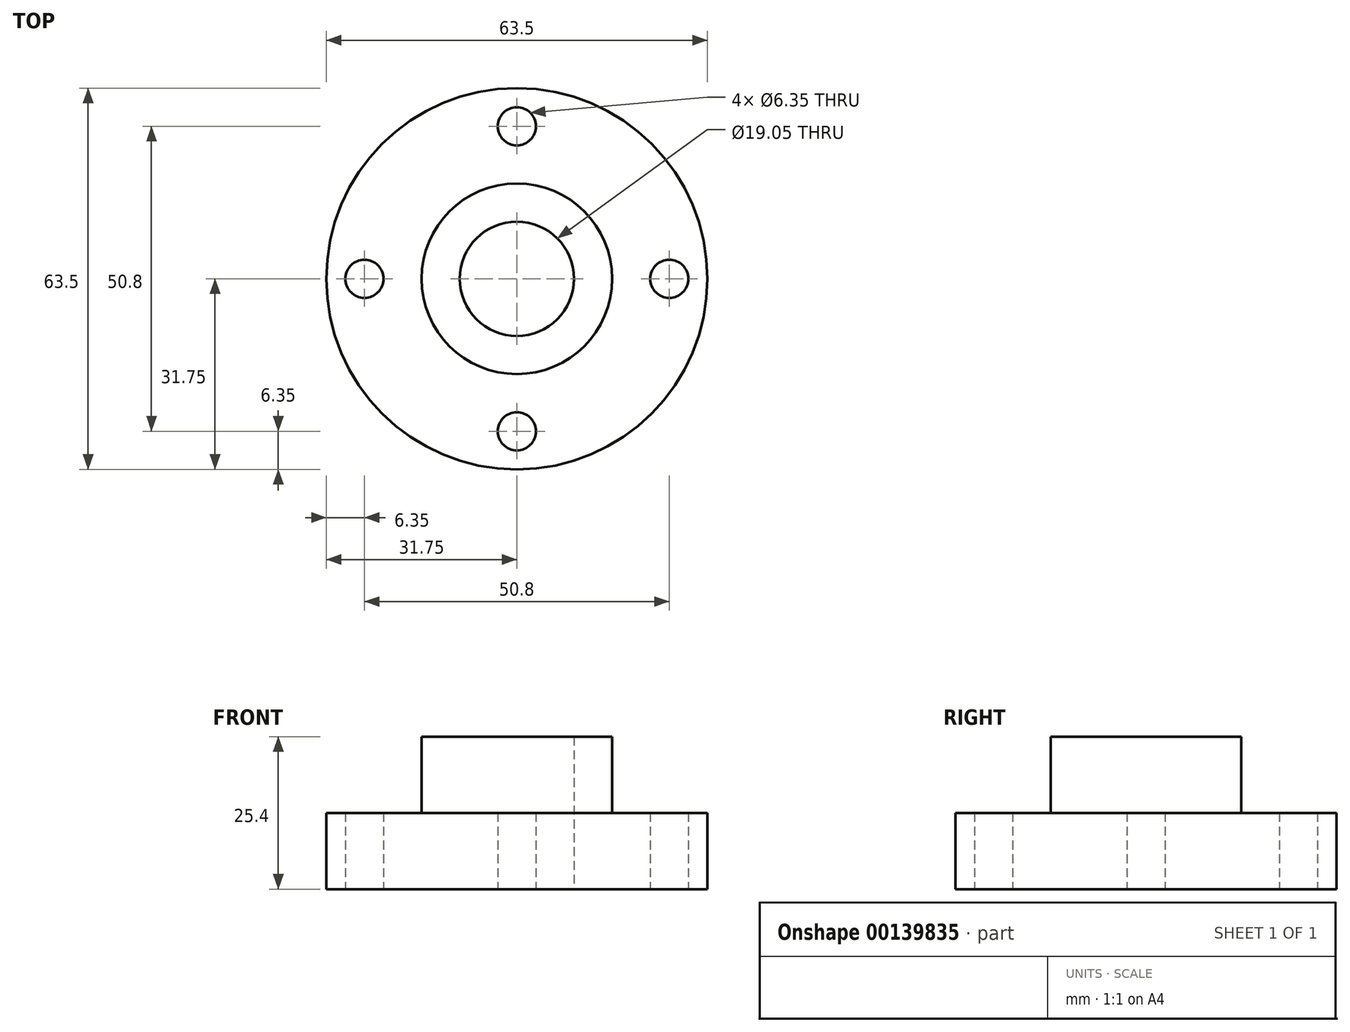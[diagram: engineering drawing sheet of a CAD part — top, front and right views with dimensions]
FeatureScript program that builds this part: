
annotation { "Feature Type Name" : "Feature", "Feature Type Description" : "" }
export const myFeature = defineFeature(function(context is Context, id is Id, definition is map)
    precondition{}
    {
        {
            var Q0;
            Q0=qCreatedBy(makeId("Top.planeOp"),FACE);
            var sketch = newSketch(context, id + "F0", { "sketchPlane" : qUnion([Q0])});
            skCircle(sketch, "E0", {"center": v(0, 0) * mm, "radius": 9.53 * mm});
            skCircle(sketch, "E1.0", {"center": v(0, 0) * mm, "radius": 15.87 * mm});
            skCircle(sketch, "E2.0", {"center": v(0, 0) * mm, "radius": 25.4 * mm});
            skCircle(sketch, "E3.0", {"center": v(0, 0) * mm, "radius": 31.75 * mm});
            skCircle(sketch, "E4", {"center": v(0, 25.4) * mm, "radius": 3.18 * mm});
            skCircle(sketch, "E5", {"center": v(25.4, 0) * mm, "radius": 3.18 * mm});
            skCircle(sketch, "E6", {"center": v(-25.4, 0) * mm, "radius": 3.18 * mm});
            skCircle(sketch, "E7", {"center": v(0, -25.4) * mm, "radius": 3.18 * mm});
            skSolve(sketch);
        }
        {
            var Q0;
            Q0 = qSketchRegion(id + "F0", true);
            var Q1;
            Q1=makeQuery(id+"F0.imprint","IMPRINT",FACE,{"disambiguationData":[TD([[makeQuery(id+"F0.imprint","IMPRINT",EDGE,{"derivedFrom":sQuery(id+"F0.wireOp",EDGE,"E1.0")}),-1.0]])]});
            extrude(context, id + "F1", {"entities" : qUnion([Q0, Q1]), "depth" : 12.7 * mm});
        }
        {
            var Q0;
            Q0=makeQuery(id+"F0.imprint","IMPRINT",FACE,{"disambiguationData":[TD([[makeQuery(id+"F0.imprint","IMPRINT",EDGE,{"derivedFrom":sQuery(id+"F0.wireOp",EDGE,"E0")}),-1.0]])]});
            extrude(context, id + "F2", {"entities" : qUnion([Q0]), "operationType" : NewBodyOperationType.ADD, "depth" : 25.4 * mm});
        }
    });
